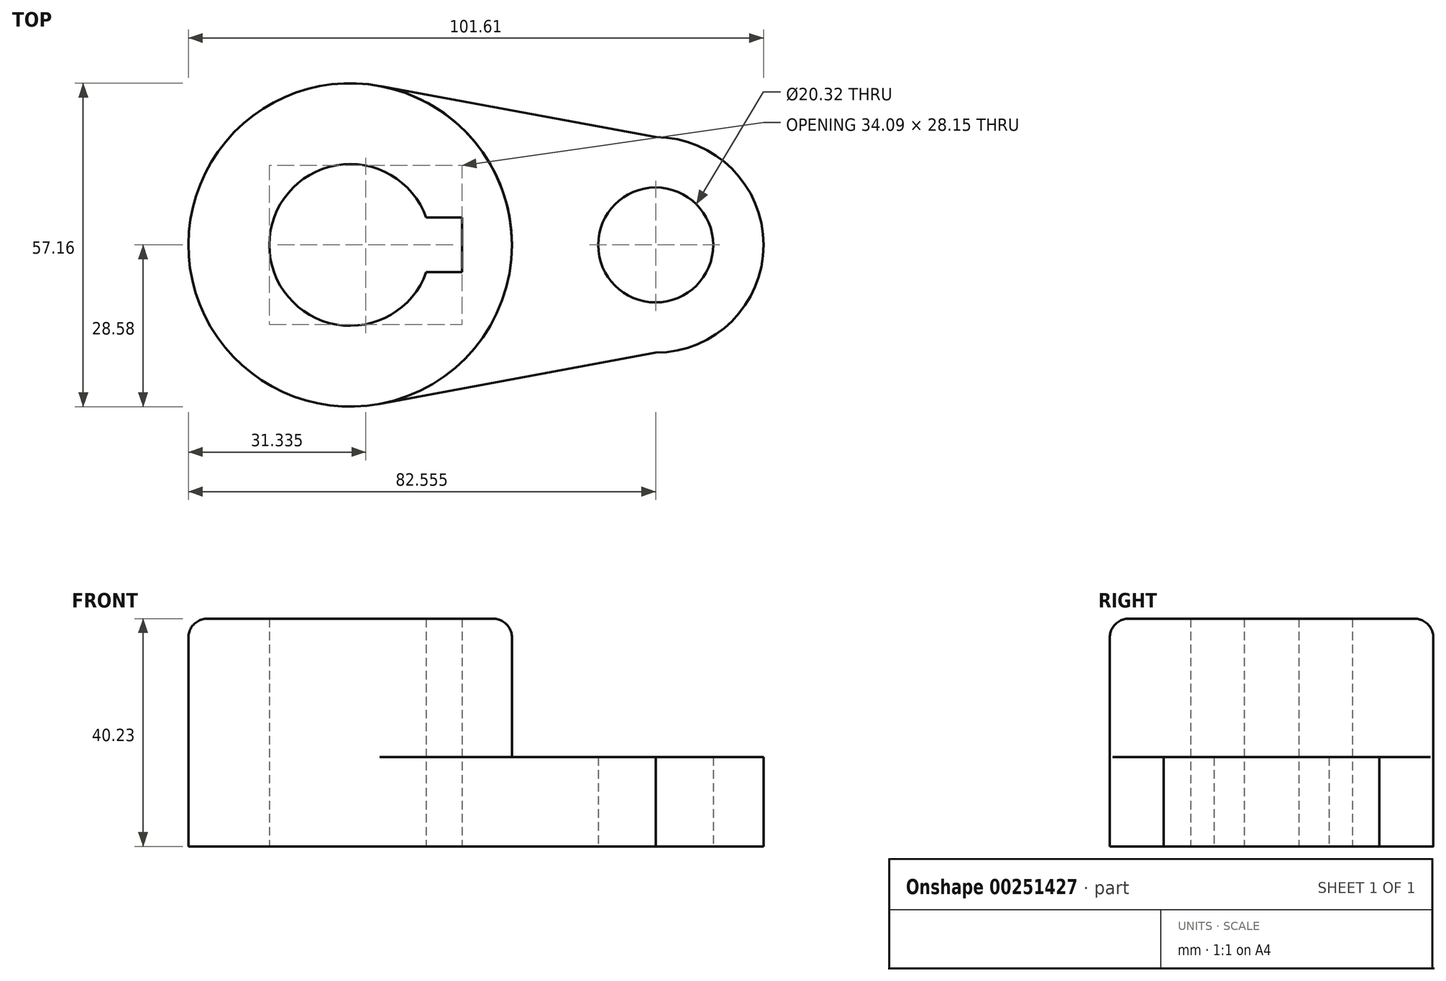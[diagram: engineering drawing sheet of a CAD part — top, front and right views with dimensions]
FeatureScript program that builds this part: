
annotation { "Feature Type Name" : "Feature", "Feature Type Description" : "" }
export const myFeature = defineFeature(function(context is Context, id is Id, definition is map)
    precondition{}
    {
        {
            var Q0;
            Q0=qCreatedBy(makeId("Top.planeOp"),FACE);
            var sketch = newSketch(context, id + "F0", { "sketchPlane" : qUnion([Q0])});
            skArc(sketch, "E0", {"start": v(13.45, 4.83) * mm, "mid": v(-14.29, 0) * mm, "end": v(13.45, -4.83) * mm});
            skCircle(sketch, "E1", {"center": v(53.98, 0) * mm, "radius": 10.16 * mm});
            skCircle(sketch, "E2", {"center": v(0, 0) * mm, "radius": 28.58 * mm});
            skCircle(sketch, "E3", {"center": v(53.98, 0) * mm, "radius": 19.05 * mm});
            skPoint(sketch, "E4.visualSharp", {"position": v(33.04, -28.58) * mm});
            skLineSegment(sketch, "E5.right", {"start": v(19.8, -4.83) * mm, "end": v(19.8, 4.83) * mm});
            skLineSegment(sketch, "E6.trimOffspring", {"start": v(13.45, 4.83) * mm, "end": v(19.8, 4.83) * mm});
            skLineSegment(sketch, "E7.trimOffspring", {"start": v(13.45, -4.83) * mm, "end": v(19.8, -4.83) * mm});
            skLineSegment(sketch, "E8", {"start": v(0, 0) * mm, "end": v(53.97, 0) * mm, "construction": true});
            skLineSegment(sketch, "E9", {"start": v(53.98, 19.05) * mm, "end": v(5.21, 28.1) * mm});
            skLineSegment(sketch, "E10", {"start": v(53.98, -19.05) * mm, "end": v(5.21, -28.1) * mm});
            skSolve(sketch);
        }
        {
            var Q0;
            Q0=makeQuery(id+"F0.imprint","IMPRINT",FACE,{"disambiguationData":[TD([[makeQuery(id+"F0.imprint","IMPRINT",EDGE,{"derivedFrom":sQuery(id+"F0.wireOp",EDGE,"E0")}),-1.0]])]});
            extrude(context, id + "F1", {"entities" : qUnion([Q0]), "depth" : 40.23 * mm});
        }
        {
            var Q0;
            {var subQ0=sQuery(id+"F0.wireOp",EDGE,"o5OdITKO-bEnJ-2VYi-a7Jk-zIUuU5JH3HSI");var subQ1=sQuery(id+"F0.wireOp",EDGE,"E2");var subQ2=makeQuery(id+"F0.imprint","INTERSECT",VERTEX,{"disambiguationData":[OD(1.0)],"derivedFrom":[subQ1,subQ0]});Q0=makeQuery(id+"F0.imprint","IMPRINT",FACE,{"disambiguationData":[TD([[makeQuery(id+"F0.imprint","IMPRINT",EDGE,{"disambiguationData":[TD([[subQ2,1.0]])],"derivedFrom":subQ1}),-1.0]])]});}
            var Q1;
            Q1=makeQuery(id+"F0.imprint","IMPRINT",FACE,{"disambiguationData":[TD([[makeQuery(id+"F0.imprint","IMPRINT",EDGE,{"derivedFrom":sQuery(id+"F0.wireOp",EDGE,"E1")}),-1.0]])]});
            extrude(context, id + "F2", {"entities" : qUnion([Q0, Q1]), "operationType" : NewBodyOperationType.ADD, "depth" : 15.77 * mm});
        }
        {
            var Q0;
            {var subQ0=sQuery(id+"F0.wireOp",EDGE,"E2");Q0=makeQuery(id+"F1.opExtrude","CAP_EDGE",EDGE,{"disambiguationData":[OSD([subQ0]),TDD([makeQuery(id+"F0.imprint","IMPRINT",EDGE,{"disambiguationData":[TD([[makeQuery(id+"F0.imprint","INTERSECT",VERTEX,{"disambiguationData":[OD(0.0)],"derivedFrom":[subQ0,sQuery(id+"F0.wireOp",EDGE,"SRnHb5uK-vhAm-8B8o-SrwD-EHZrL22LgCVp")]}),1.0]])],"derivedFrom":subQ0})])],"isStart":false});}
            var Q1;
            Q1=makeQuery(id+"F1.opExtrude","CAP_EDGE",EDGE,{"disambiguationData":[OSD([sQuery(id+"F0.wireOp",EDGE,"SRnHb5uK-vhAm-8B8o-SrwD-EHZrL22LgCVp")])],"isStart":false});
            var Q2;
            {var subQ0=sQuery(id+"F0.wireOp",EDGE,"E2");Q2=makeQuery(id+"F1.opExtrude","CAP_EDGE",EDGE,{"disambiguationData":[OSD([subQ0]),TDD([makeQuery(id+"F0.imprint","IMPRINT",EDGE,{"disambiguationData":[TD([[makeQuery(id+"F0.imprint","INTERSECT",VERTEX,{"disambiguationData":[OD(1.0)],"derivedFrom":[subQ0,sQuery(id+"F0.wireOp",EDGE,"o5OdITKO-bEnJ-2VYi-a7Jk-zIUuU5JH3HSI")]}),1.0]])],"derivedFrom":subQ0})])],"isStart":false});}
            var Q3;
            Q3=makeQuery(id+"F1.opExtrude","CAP_EDGE",EDGE,{"disambiguationData":[OSD([sQuery(id+"F0.wireOp",EDGE,"o5OdITKO-bEnJ-2VYi-a7Jk-zIUuU5JH3HSI")])],"isStart":false});
            fillet(context, id + "F3", {"entities" : qUnion([Q0, Q1, Q2, Q3]), "radius" : 3.3 * mm, "tangentPropagation" : true, "allowEdgeOverflow" : false});
        }
    });
